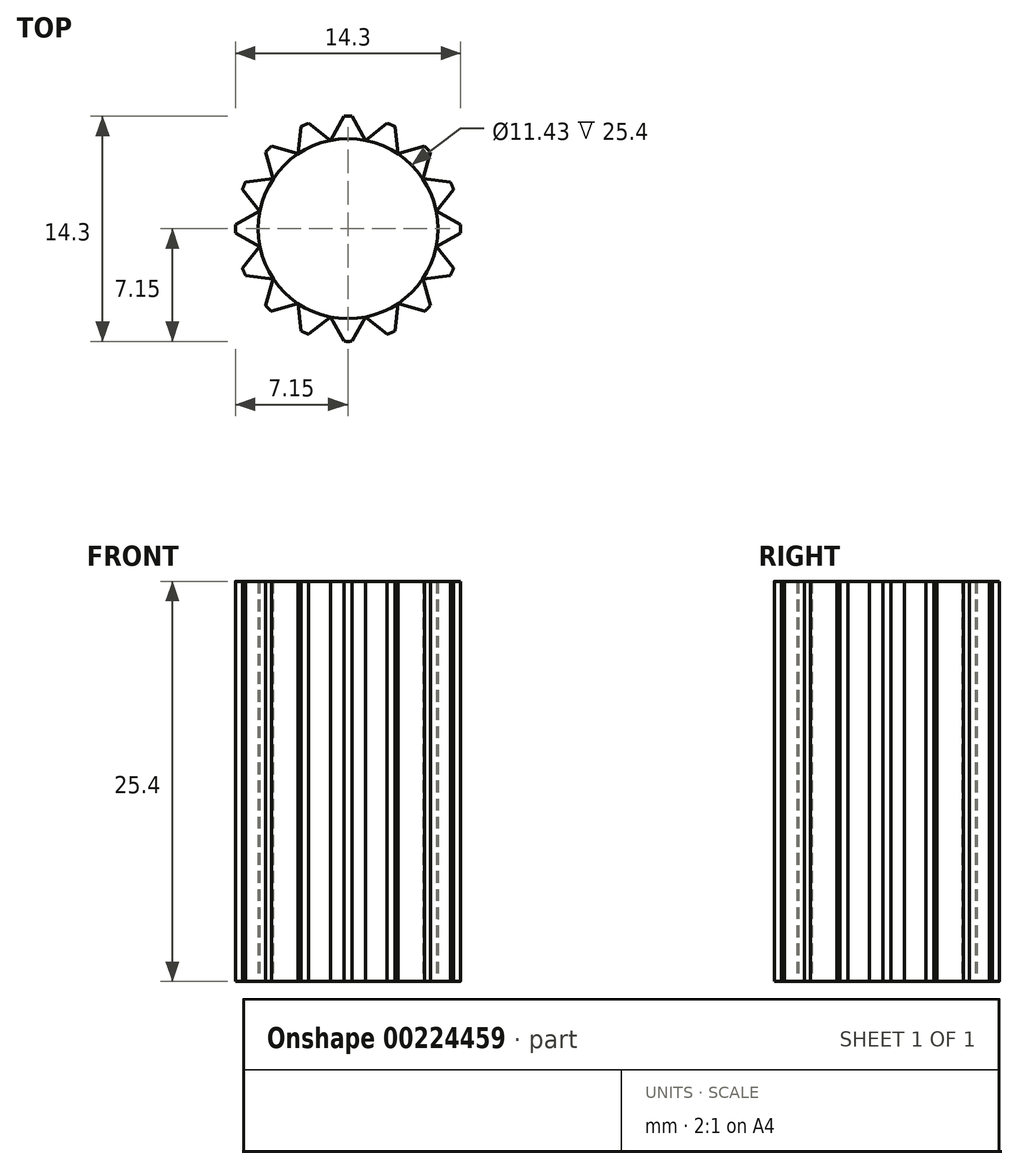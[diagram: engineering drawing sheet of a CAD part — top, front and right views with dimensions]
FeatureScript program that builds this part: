
annotation { "Feature Type Name" : "Feature", "Feature Type Description" : "" }
export const myFeature = defineFeature(function(context is Context, id is Id, definition is map)
    precondition{}
    {
        {
            var Q0;
            Q0=qCreatedBy(makeId("Top.planeOp"),FACE);
            var sketch = newSketch(context, id + "F0", { "sketchPlane" : qUnion([Q0])});
            skCircle(sketch, "E0", {"center": v(0, 0) * mm, "radius": 3.17 * mm});
            skArc(sketch, "E1", {"start": v(0.27, 7.15) * mm, "mid": v(0, 7.15) * mm, "end": v(-0.27, 7.15) * mm});
            skCircle(sketch, "E2", {"center": v(0, 0) * mm, "radius": 5.72 * mm});
            skLineSegment(sketch, "E3", {"start": v(1.12, 5.6) * mm, "end": v(0.27, 7.15) * mm});
            skLineSegment(sketch, "E4", {"start": v(-1.12, 5.6) * mm, "end": v(-0.27, 7.15) * mm});
            skArc(sketch, "E5.1.0", {"start": v(-2.49, 6.7) * mm, "mid": v(-2.74, 6.6) * mm, "end": v(-2.98, 6.5) * mm});
            skLineSegment(sketch, "E5.1.1", {"start": v(-1.1, 5.6) * mm, "end": v(-2.49, 6.7) * mm});
            skLineSegment(sketch, "E5.1.2", {"start": v(-3.18, 4.75) * mm, "end": v(-2.98, 6.5) * mm});
            skArc(sketch, "E5.2.0", {"start": v(-4.86, 5.24) * mm, "mid": v(-5.06, 5.06) * mm, "end": v(-5.24, 4.86) * mm});
            skLineSegment(sketch, "E5.2.1", {"start": v(-3.17, 4.76) * mm, "end": v(-4.86, 5.24) * mm});
            skLineSegment(sketch, "E5.2.2", {"start": v(-4.76, 3.17) * mm, "end": v(-5.24, 4.86) * mm});
            skArc(sketch, "E5.3.0", {"start": v(-6.5, 2.98) * mm, "mid": v(-6.6, 2.74) * mm, "end": v(-6.7, 2.49) * mm});
            skLineSegment(sketch, "E5.3.1", {"start": v(-4.75, 3.18) * mm, "end": v(-6.5, 2.98) * mm});
            skLineSegment(sketch, "E5.3.2", {"start": v(-5.6, 1.1) * mm, "end": v(-6.7, 2.49) * mm});
            skArc(sketch, "E5.4.0", {"start": v(-7.15, 0.27) * mm, "mid": v(-7.15, 0) * mm, "end": v(-7.15, -0.27) * mm});
            skLineSegment(sketch, "E5.4.1", {"start": v(-5.6, 1.12) * mm, "end": v(-7.15, 0.27) * mm});
            skLineSegment(sketch, "E5.4.2", {"start": v(-5.6, -1.12) * mm, "end": v(-7.15, -0.27) * mm});
            skArc(sketch, "E5.5.0", {"start": v(-6.7, -2.49) * mm, "mid": v(-6.6, -2.74) * mm, "end": v(-6.5, -2.98) * mm});
            skLineSegment(sketch, "E5.5.1", {"start": v(-5.6, -1.1) * mm, "end": v(-6.7, -2.49) * mm});
            skLineSegment(sketch, "E5.5.2", {"start": v(-4.75, -3.18) * mm, "end": v(-6.5, -2.98) * mm});
            skArc(sketch, "E5.6.0", {"start": v(-5.24, -4.86) * mm, "mid": v(-5.06, -5.06) * mm, "end": v(-4.86, -5.24) * mm});
            skLineSegment(sketch, "E5.6.1", {"start": v(-4.76, -3.17) * mm, "end": v(-5.24, -4.86) * mm});
            skLineSegment(sketch, "E5.6.2", {"start": v(-3.17, -4.76) * mm, "end": v(-4.86, -5.24) * mm});
            skArc(sketch, "E5.7.0", {"start": v(-2.98, -6.5) * mm, "mid": v(-2.74, -6.6) * mm, "end": v(-2.49, -6.7) * mm});
            skLineSegment(sketch, "E5.7.1", {"start": v(-3.18, -4.75) * mm, "end": v(-2.98, -6.5) * mm});
            skLineSegment(sketch, "E5.7.2", {"start": v(-1.1, -5.6) * mm, "end": v(-2.49, -6.7) * mm});
            skArc(sketch, "E5.8.0", {"start": v(-0.27, -7.15) * mm, "mid": v(0, -7.15) * mm, "end": v(0.27, -7.15) * mm});
            skLineSegment(sketch, "E5.8.1", {"start": v(-1.12, -5.6) * mm, "end": v(-0.27, -7.15) * mm});
            skLineSegment(sketch, "E5.8.2", {"start": v(1.12, -5.6) * mm, "end": v(0.27, -7.15) * mm});
            skArc(sketch, "E5.9.0", {"start": v(2.49, -6.7) * mm, "mid": v(2.74, -6.6) * mm, "end": v(2.98, -6.5) * mm});
            skLineSegment(sketch, "E5.9.1", {"start": v(1.1, -5.6) * mm, "end": v(2.49, -6.7) * mm});
            skLineSegment(sketch, "E5.9.2", {"start": v(3.18, -4.75) * mm, "end": v(2.98, -6.5) * mm});
            skArc(sketch, "E5.10.0", {"start": v(4.86, -5.24) * mm, "mid": v(5.06, -5.06) * mm, "end": v(5.24, -4.86) * mm});
            skLineSegment(sketch, "E5.10.1", {"start": v(3.17, -4.76) * mm, "end": v(4.86, -5.24) * mm});
            skLineSegment(sketch, "E5.10.2", {"start": v(4.76, -3.17) * mm, "end": v(5.24, -4.86) * mm});
            skArc(sketch, "E5.11.0", {"start": v(6.5, -2.98) * mm, "mid": v(6.6, -2.74) * mm, "end": v(6.7, -2.49) * mm});
            skLineSegment(sketch, "E5.11.1", {"start": v(4.75, -3.18) * mm, "end": v(6.5, -2.98) * mm});
            skLineSegment(sketch, "E5.11.2", {"start": v(5.6, -1.1) * mm, "end": v(6.7, -2.49) * mm});
            skArc(sketch, "E5.12.0", {"start": v(7.15, -0.27) * mm, "mid": v(7.15, 0) * mm, "end": v(7.15, 0.27) * mm});
            skLineSegment(sketch, "E5.12.1", {"start": v(5.6, -1.12) * mm, "end": v(7.15, -0.27) * mm});
            skLineSegment(sketch, "E5.12.2", {"start": v(5.6, 1.12) * mm, "end": v(7.15, 0.27) * mm});
            skArc(sketch, "E5.13.0", {"start": v(6.7, 2.49) * mm, "mid": v(6.6, 2.74) * mm, "end": v(6.5, 2.98) * mm});
            skLineSegment(sketch, "E5.13.1", {"start": v(5.6, 1.1) * mm, "end": v(6.7, 2.49) * mm});
            skLineSegment(sketch, "E5.13.2", {"start": v(4.75, 3.18) * mm, "end": v(6.5, 2.98) * mm});
            skArc(sketch, "E5.14.0", {"start": v(5.24, 4.86) * mm, "mid": v(5.06, 5.06) * mm, "end": v(4.86, 5.24) * mm});
            skLineSegment(sketch, "E5.14.1", {"start": v(4.76, 3.17) * mm, "end": v(5.24, 4.86) * mm});
            skLineSegment(sketch, "E5.14.2", {"start": v(3.17, 4.76) * mm, "end": v(4.86, 5.24) * mm});
            skArc(sketch, "E5.15.0", {"start": v(2.98, 6.5) * mm, "mid": v(2.74, 6.6) * mm, "end": v(2.49, 6.7) * mm});
            skLineSegment(sketch, "E5.15.1", {"start": v(3.18, 4.75) * mm, "end": v(2.98, 6.5) * mm});
            skLineSegment(sketch, "E5.15.2", {"start": v(1.1, 5.6) * mm, "end": v(2.49, 6.7) * mm});
            skSolve(sketch);
        }
        {
            var Q0;
            Q0 = qSketchRegion(id + "F0", true);
            extrude(context, id + "F1", {"entities" : qUnion([Q0]), "depth" : 25.4 * mm});
        }
    });
